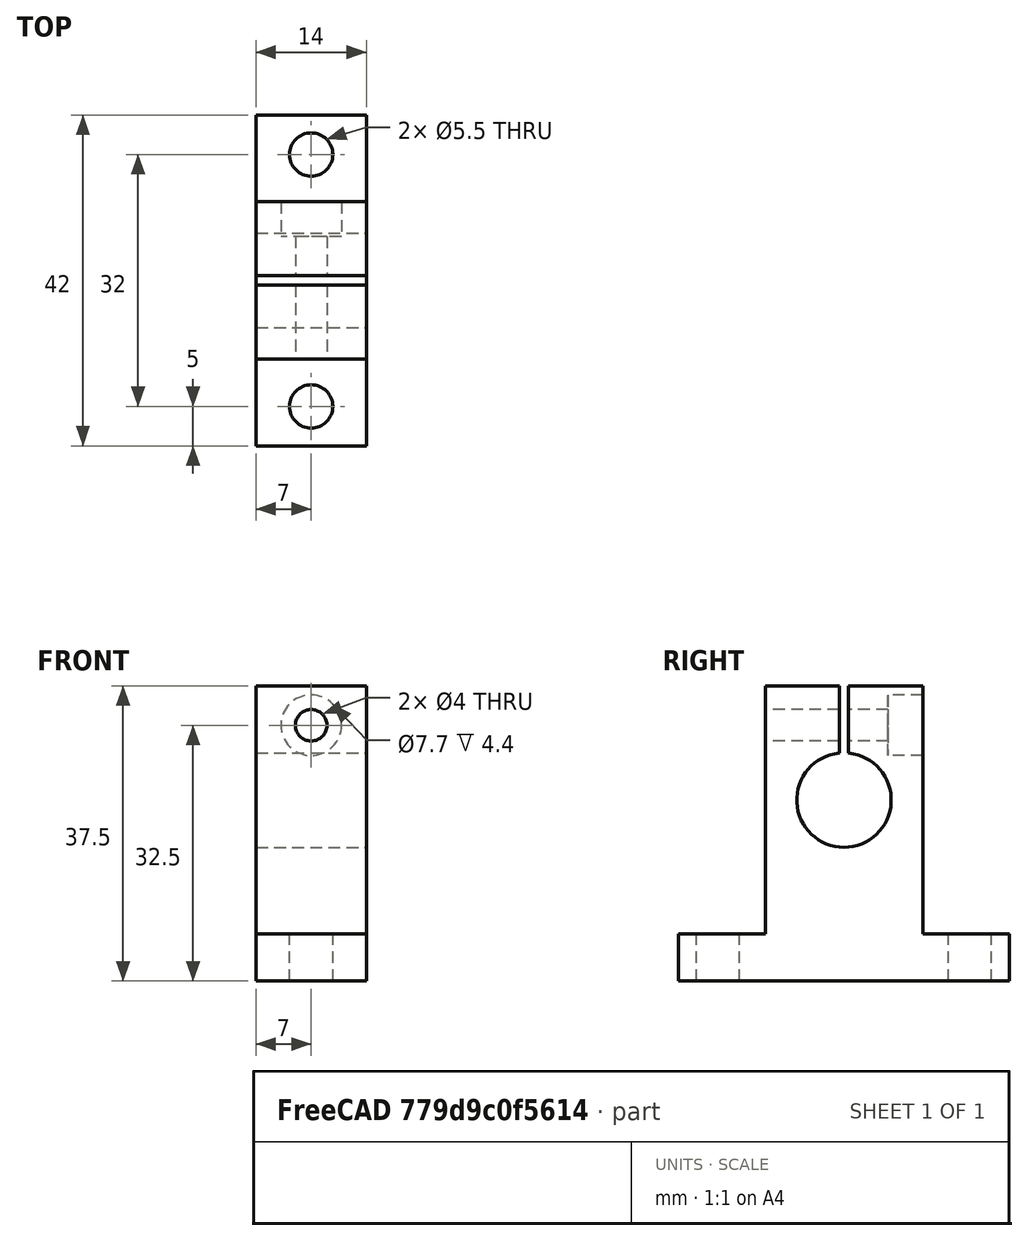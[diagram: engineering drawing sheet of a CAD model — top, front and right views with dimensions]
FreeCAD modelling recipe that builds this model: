
FCSTD DOCUMENT  (FreeCAD 0.15R4671 (Git))
Label: sk12
License: All rights reserved
LicenseURL: http://en.wikipedia.org/wiki/All_rights_reserved
objects: Part::Cylinder×5, Part::Box×4, Part::Cut×3, Part::Fuse×2, Part::MultiFuse×1
note: 15 computed .brp shape members not serialized (recipe doc carries the construction recipe); baked Part::Feature solids carry a one-line shape summary decoded from their .brp

FEATURE [Part::Box] total_box
  Height = 37.5
  Length = 14
  Placement = pos=(0,-21,0) rot=(0,0,1;0rad)
  Width = 42
FEATURE [Part::Box] side_box_r
  Height = 31.5
  Length = 14
  Placement = pos=(0,10,6) rot=(0,0,1;0rad)
  Width = 11
FEATURE [Part::Box] side_box_l
  Height = 31.5
  Length = 14
  Placement = pos=(0,-21,6) rot=(0,0,1;0rad)
  Width = 11
FEATURE [Part::Fuse] side_boxes
  Base = -> side_box_r
  Tool = -> side_box_l
FEATURE [Part::Cut] sk_shape
  Base = -> total_box
  Tool = -> side_boxes
FEATURE [Part::Cylinder] shaft_hole
  Angle = 360
  Height = 16
  Placement = pos=(-1,0,23) rot=(0,1,0;1.5708rad)
  Radius = 6
FEATURE [Part::Box] up_sep
  Height = 15.5
  Length = 16
  Placement = pos=(-1,-0.6,24) rot=(0,0,1;0rad)
  Width = 1.2
FEATURE [Part::Cylinder] tbolt_shaft
  Angle = 360
  Height = 22
  Placement = pos=(7,11,32.5) rot=(1,0,0;1.5708rad)
  Radius = 2
FEATURE [Part::Cylinder] tbolt_head
  Angle = 360
  Height = 5.4
  Placement = pos=(7,11,32.5) rot=(1,0,0;1.5708rad)
  Radius = 3.85
FEATURE [Part::MultiFuse] fuse_shaft_holes
  Shapes = -> [tbolt_head,tbolt_shaft,up_sep,shaft_hole]
FEATURE [Part::Cut] sk_shape_w_holes
  Base = -> sk_shape
  Tool = -> fuse_shaft_holes
FEATURE [Part::Cylinder] mbolt_sh_r
  Angle = 360
  Height = 8
  Placement = pos=(7,16,-1) rot=(0,0,1;0rad)
  Radius = 2.75
FEATURE [Part::Cylinder] mbolt_sh_l
  Angle = 360
  Height = 8
  Placement = pos=(7,-16,-1) rot=(0,0,1;0rad)
  Radius = 2.75
FEATURE [Part::Fuse] mbolts_sh
  Base = -> mbolt_sh_r
  Tool = -> mbolt_sh_l
FEATURE [Part::Cut] sk_final
  Base = -> sk_shape_w_holes
  Tool = -> mbolts_sh
